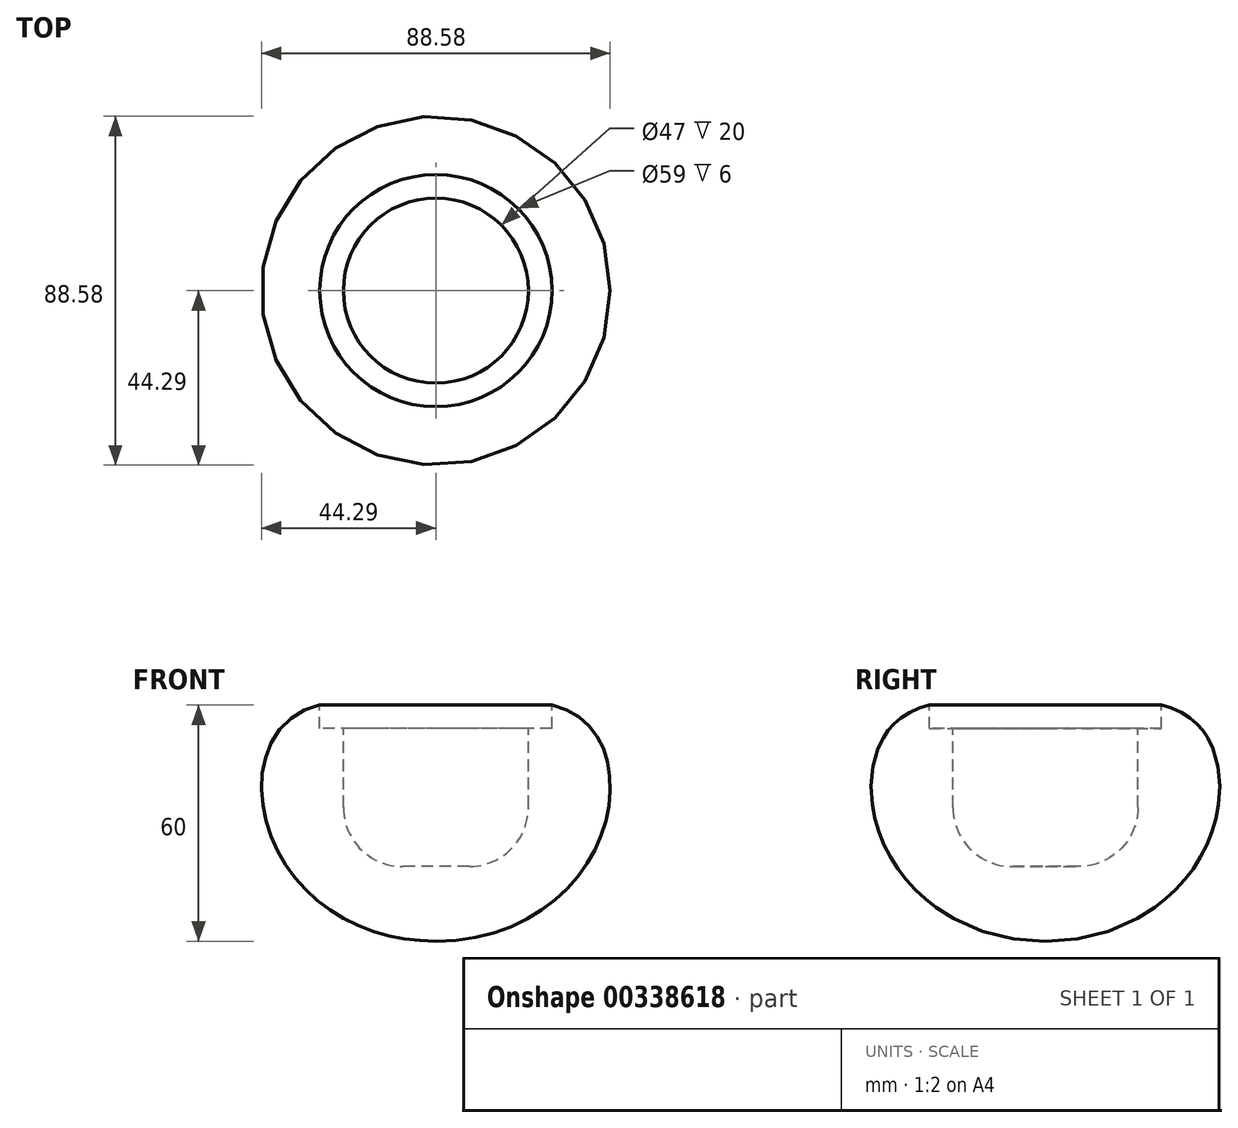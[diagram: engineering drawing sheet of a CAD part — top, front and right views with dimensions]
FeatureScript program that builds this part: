
annotation { "Feature Type Name" : "Feature", "Feature Type Description" : "" }
export const myFeature = defineFeature(function(context is Context, id is Id, definition is map)
    precondition{}
    {
        {
            var Q0;
            Q0=qCreatedBy(makeId("Front.planeOp"),FACE);
            var sketch = newSketch(context, id + "F0", { "sketchPlane" : qUnion([Q0])});
            skLineSegment(sketch, "E0", {"start": v(23.5, 29.69) * mm, "end": v(29.5, 29.69) * mm});
            skLineSegment(sketch, "E1", {"start": v(29.5, 29.69) * mm, "end": v(29.5, 35.69) * mm});
            skLineSegment(sketch, "E2", {"start": v(23.5, 29.69) * mm, "end": v(23.5, 9.69) * mm});
            skLineSegment(sketch, "E3", {"start": v(23.5, 9.69) * mm, "end": v(23.5, 9.69) * mm});
            skLineSegment(sketch, "E4", {"start": v(8.5, -5.31) * mm, "end": v(0, -5.31) * mm});
            skPoint(sketch, "E5.visualSharp", {"position": v(23.5, -5.31) * mm});
            skArc(sketch, "E5.filletArc", {"start": v(8.5, -5.31) * mm, "mid": v(19.1, -0.92) * mm, "end": v(23.5, 9.69) * mm});
            skLineSegment(sketch, "E6", {"start": v(43, 38.22) * mm, "end": v(43, -53.52) * mm, "construction": true});
            skLineSegment(sketch, "E7", {"start": v(0, 64.06) * mm, "end": v(0, -46.95) * mm, "construction": true});
            skLineSegment(sketch, "E8", {"start": v(29.5, 35.69) * mm, "end": v(152.51, 35.69) * mm, "construction": true});
            skLineSegment(sketch, "E9", {"start": v(0, -24.31) * mm, "end": v(151.95, -24.31) * mm, "construction": true});
            skPoint(sketch, "E10", {"position": v(43, 35.69) * mm});
            skPoint(sketch, "E11", {"position": v(43, -24.31) * mm});
            skPoint(sketch, "E12", {"position": v(43, 5.69) * mm});
            skFitSpline(sketch, "E13", {"points": [v(29.5, 35.69) * mm, v(43, 5.69) * mm, v(0, -24.31) * mm], "startDerivative": vector(91.63, -20.36) * mm, "endDerivative": vector(-121.99, 0) * mm});
            skPoint(sketch, "E14", {"position": v(29.5, 32.69) * mm});
            skLineSegment(sketch, "E15", {"start": v(0, -5.31) * mm, "end": v(0, -24.31) * mm});
            skSolve(sketch);
        }
        {
            var Q0;
            Q0=makeQuery(id+"F0.imprint","IMPRINT",FACE,{"disambiguationData":[TD([[makeQuery(id+"F0.imprint","IMPRINT",EDGE,{"derivedFrom":sQuery(id+"F0.wireOp",EDGE,"E0")}),-1.0]])]});
            var Q1;
            Q1=sQuery(id+"F0.wireOp",EDGE,"E7");
            revolve(context, id + "F1", {"entities" : qUnion([Q0]), "axis" : qUnion([Q1]), "revolveType" : RevolveType.FULL});
        }
    });
